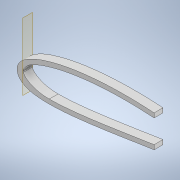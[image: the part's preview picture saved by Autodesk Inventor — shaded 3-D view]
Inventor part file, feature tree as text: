
AUTODESK INVENTOR PART (.ipt)
format: ipt  version: 2022.3 (Build 263350000, 350)  size: 447,488 bytes
history: native  units: mm
features: sketch x5, extrude x4, thicken_offset x3, shell x1, plane x1, other x1, projected_geometry x1
ambient origin geometry x8: Origin, YZ Plane, XZ Plane, XY Plane, X Axis, Y Axis, Z Axis, Center Point
bodies: Solid1 (feature_tree)
feature tree (16):
  extrude  "Extrusion1"  Depth=3.0mm
  shell  "Shell1"  Thickness=1.0mm
  thicken_offset  "Thicken1"
  extrude  "Extrusion27"  TaperAngle=0.0deg  [1 undecoded]
  thicken_offset  "Thicken3"
  extrude  "Extrusion29"  Depth=30.0mm
  plane  "Work Plane5"
  other  "Bend Part2"
  thicken_offset  "Thicken5"
  extrude  "Extrusion31"  Depth=10.0mm TaperAngle=0.0deg
  sketch  "Sketch3"  dims[d0=10.0mm d1=0.0mm d2=3.0mm d159=1.0mm d160=2.0mm]
  sketch  "Sketch48"  dims[d236=190.0mm d237=0.0mm d238=0.0mm]
  sketch  "Sketch55"  dims[d249=2.0mm d250=1.0mm d254=30.0mm]
  projected_geometry  "Projected Loop32"
  sketch  "Sketch57"  dims[d255=8.0mm d256=10.0mm d257=0.0mm]
  sketch  "Sketch59"  dims[d262=10.0mm d263=2.094395mm d264=1.0mm d265=1.0mm d272=150.0mm d273=100.0mm d274=0.0mm]
note: 1 required parameter value undecoded (feature->parameter linkage not recoverable at this tier; creation-order binding heuristic only, values carry confidence <= 0.55)
